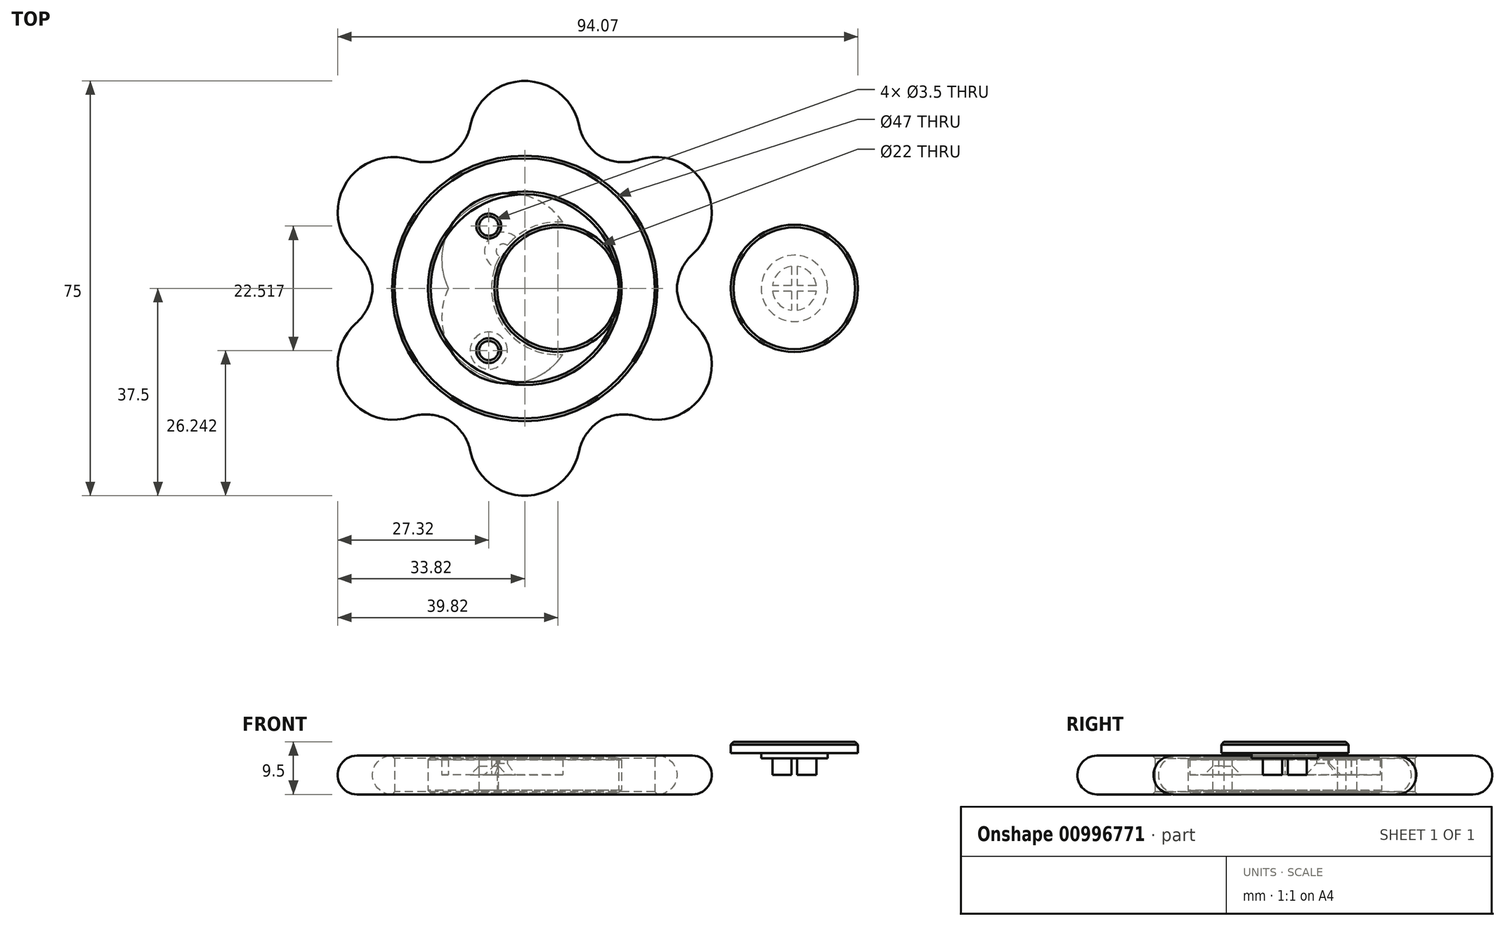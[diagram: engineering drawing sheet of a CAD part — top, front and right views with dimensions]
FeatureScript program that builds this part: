
annotation { "Feature Type Name" : "Feature", "Feature Type Description" : "" }
export const myFeature = defineFeature(function(context is Context, id is Id, definition is map)
    precondition{}
    {
        {
            var Q0;
            Q0=qCreatedBy(makeId("Top.planeOp"),FACE);
            var sketch = newSketch(context, id + "F0", { "sketchPlane" : qUnion([Q0])});
            skCircle(sketch, "E0", {"center": v(0, 0) * mm, "radius": 17.5 * mm});
            skCircle(sketch, "E1", {"center": v(6, 0) * mm, "radius": 11 * mm});
            skLineSegment(sketch, "E2", {"start": v(0, 0) * mm, "end": v(13.77, 19.66) * mm});
            skLineSegment(sketch, "E3", {"start": v(0, 0) * mm, "end": v(14.89, -21.26) * mm});
            skSolve(sketch);
        }
        {
            var Q0;
            Q0 = qSketchRegion(id + "F0", true);
            var Q1;
            {var subQ0=sQuery(id+"F0.wireOp",EDGE,"7888d7e4-cc9e-4509-8198-0eb2202acd58");var subQ1=sQuery(id+"F0.wireOp",EDGE,"E0");var subQ2=makeQuery(id+"F0.imprint","INTERSECT",VERTEX,{"derivedFrom":[subQ1,subQ0]});Q1=makeQuery(id+"F0.imprint","IMPRINT",FACE,{"disambiguationData":[TD([[makeQuery(id+"F0.imprint","IMPRINT",EDGE,{"disambiguationData":[TD([[subQ2,1.0]])],"derivedFrom":subQ1}),1.0]])]});}
            extrude(context, id + "F1", {"entities" : qUnion([Q0, Q1]), "depth" : 3.25 * mm, "offsetDistance" : 25 * mm, "hasSecondDirection" : true, "secondDirectionOppositeDirection" : true, "secondDirectionDepth" : 3.25 * mm});
        }
        {
            var Q0;
            Q0=qCreatedBy(makeId("Top.planeOp"),FACE);
            var sketch = newSketch(context, id + "F2", { "sketchPlane" : qUnion([Q0])});
            skCircle(sketch, "E4", {"center": v(0, 0) * mm, "radius": 23.5 * mm});
            skCircle(sketch, "E5", {"center": v(0, 0) * mm, "radius": 27.5 * mm});
            skArc(sketch, "E6", {"start": v(9.83, 25.68) * mm, "mid": v(0, 37.5) * mm, "end": v(-9.83, 25.68) * mm});
            skArc(sketch, "E7.1.0", {"start": v(-17.32, 21.36) * mm, "mid": v(-32.48, 18.75) * mm, "end": v(-27.16, 4.33) * mm});
            skArc(sketch, "E7.2.0", {"start": v(-27.16, -4.33) * mm, "mid": v(-32.48, -18.75) * mm, "end": v(-17.32, -21.36) * mm});
            skArc(sketch, "E7.3.0", {"start": v(-9.83, -25.68) * mm, "mid": v(0, -37.5) * mm, "end": v(9.83, -25.68) * mm});
            skArc(sketch, "E7.4.0", {"start": v(17.32, -21.36) * mm, "mid": v(32.48, -18.75) * mm, "end": v(27.16, -4.33) * mm});
            skArc(sketch, "E7.5.0", {"start": v(27.16, 4.33) * mm, "mid": v(32.48, 18.75) * mm, "end": v(17.32, 21.36) * mm});
            skPoint(sketch, "E8.orphan", {"position": v(8.33, 21.97) * mm});
            skPoint(sketch, "E9.orphan", {"position": v(-8.33, 21.97) * mm});
            skPoint(sketch, "E10.orphan", {"position": v(-14.86, 18.2) * mm});
            skPoint(sketch, "E11.orphan", {"position": v(-23.2, 3.77) * mm});
            skPoint(sketch, "E12.orphan", {"position": v(-23.2, -3.77) * mm});
            skPoint(sketch, "E13.orphan", {"position": v(-14.86, -18.2) * mm});
            skPoint(sketch, "E14.orphan", {"position": v(-8.33, -21.97) * mm});
            skPoint(sketch, "E15.orphan", {"position": v(8.33, -21.97) * mm});
            skPoint(sketch, "E16.orphan", {"position": v(14.86, -18.2) * mm});
            skPoint(sketch, "E17.orphan", {"position": v(23.2, -3.77) * mm});
            skPoint(sketch, "E18.orphan", {"position": v(23.2, 3.77) * mm});
            skPoint(sketch, "E19.orphan", {"position": v(14.86, 18.2) * mm});
            skSolve(sketch);
        }
        {
            var Q0;
            Q0 = qSketchRegion(id + "F2", true);
            extrude(context, id + "F3", {"entities" : qUnion([Q0]), "depth" : 3.5 * mm, "offsetDistance" : 25 * mm, "hasSecondDirection" : true, "secondDirectionOppositeDirection" : true, "secondDirectionDepth" : 3.5 * mm});
        }
        {
            var Q0;
            {var subQ0=sQuery(id+"F2.wireOp",EDGE,"E7.1.0");var subQ1=sQuery(id+"F2.wireOp",EDGE,"E5");Q0=makeQuery(id+"F3.opExtrude","SWEPT_EDGE",EDGE,{"disambiguationData":[OSD([subQ1,subQ0]),TDD([makeQuery(id+"F2.imprint","INTERSECT",VERTEX,{"disambiguationData":[OD(0.0)],"derivedFrom":[subQ1,subQ0]})])]});}
            var Q1;
            {var subQ0=sQuery(id+"F2.wireOp",EDGE,"E6");var subQ1=sQuery(id+"F2.wireOp",EDGE,"E5");Q1=makeQuery(id+"F3.opExtrude","SWEPT_EDGE",EDGE,{"disambiguationData":[OSD([subQ1,subQ0]),TDD([makeQuery(id+"F2.imprint","INTERSECT",VERTEX,{"disambiguationData":[OD(1.0)],"derivedFrom":[subQ1,subQ0]})])]});}
            var Q2;
            {var subQ0=sQuery(id+"F2.wireOp",EDGE,"E7.1.0");var subQ1=sQuery(id+"F2.wireOp",EDGE,"E5");Q2=makeQuery(id+"F3.opExtrude","SWEPT_EDGE",EDGE,{"disambiguationData":[OSD([subQ1,subQ0]),TDD([makeQuery(id+"F2.imprint","INTERSECT",VERTEX,{"disambiguationData":[OD(1.0)],"derivedFrom":[subQ1,subQ0]})])]});}
            var Q3;
            {var subQ0=sQuery(id+"F2.wireOp",EDGE,"E7.2.0");var subQ1=sQuery(id+"F2.wireOp",EDGE,"E5");Q3=makeQuery(id+"F3.opExtrude","SWEPT_EDGE",EDGE,{"disambiguationData":[OSD([subQ1,subQ0]),TDD([makeQuery(id+"F2.imprint","INTERSECT",VERTEX,{"disambiguationData":[OD(0.0)],"derivedFrom":[subQ1,subQ0]})])]});}
            var Q4;
            {var subQ0=sQuery(id+"F2.wireOp",EDGE,"E7.2.0");var subQ1=sQuery(id+"F2.wireOp",EDGE,"E5");Q4=makeQuery(id+"F3.opExtrude","SWEPT_EDGE",EDGE,{"disambiguationData":[OSD([subQ1,subQ0]),TDD([makeQuery(id+"F2.imprint","INTERSECT",VERTEX,{"disambiguationData":[OD(1.0)],"derivedFrom":[subQ1,subQ0]})])]});}
            var Q5;
            {var subQ0=sQuery(id+"F2.wireOp",EDGE,"E7.3.0");var subQ1=sQuery(id+"F2.wireOp",EDGE,"E5");Q5=makeQuery(id+"F3.opExtrude","SWEPT_EDGE",EDGE,{"disambiguationData":[OSD([subQ1,subQ0]),TDD([makeQuery(id+"F2.imprint","INTERSECT",VERTEX,{"disambiguationData":[OD(0.0)],"derivedFrom":[subQ1,subQ0]})])]});}
            var Q6;
            {var subQ0=sQuery(id+"F2.wireOp",EDGE,"E7.3.0");var subQ1=sQuery(id+"F2.wireOp",EDGE,"E5");Q6=makeQuery(id+"F3.opExtrude","SWEPT_EDGE",EDGE,{"disambiguationData":[OSD([subQ1,subQ0]),TDD([makeQuery(id+"F2.imprint","INTERSECT",VERTEX,{"disambiguationData":[OD(1.0)],"derivedFrom":[subQ1,subQ0]})])]});}
            var Q7;
            {var subQ0=sQuery(id+"F2.wireOp",EDGE,"E7.4.0");var subQ1=sQuery(id+"F2.wireOp",EDGE,"E5");Q7=makeQuery(id+"F3.opExtrude","SWEPT_EDGE",EDGE,{"disambiguationData":[OSD([subQ1,subQ0]),TDD([makeQuery(id+"F2.imprint","INTERSECT",VERTEX,{"disambiguationData":[OD(0.0)],"derivedFrom":[subQ1,subQ0]})])]});}
            var Q8;
            {var subQ0=sQuery(id+"F2.wireOp",EDGE,"E7.4.0");var subQ1=sQuery(id+"F2.wireOp",EDGE,"E5");Q8=makeQuery(id+"F3.opExtrude","SWEPT_EDGE",EDGE,{"disambiguationData":[OSD([subQ1,subQ0]),TDD([makeQuery(id+"F2.imprint","INTERSECT",VERTEX,{"disambiguationData":[OD(1.0)],"derivedFrom":[subQ1,subQ0]})])]});}
            var Q9;
            {var subQ0=sQuery(id+"F2.wireOp",EDGE,"E7.5.0");var subQ1=sQuery(id+"F2.wireOp",EDGE,"E5");Q9=makeQuery(id+"F3.opExtrude","SWEPT_EDGE",EDGE,{"disambiguationData":[OSD([subQ1,subQ0]),TDD([makeQuery(id+"F2.imprint","INTERSECT",VERTEX,{"disambiguationData":[OD(0.0)],"derivedFrom":[subQ1,subQ0]})])]});}
            var Q10;
            {var subQ0=sQuery(id+"F2.wireOp",EDGE,"E7.5.0");var subQ1=sQuery(id+"F2.wireOp",EDGE,"E5");Q10=makeQuery(id+"F3.opExtrude","SWEPT_EDGE",EDGE,{"disambiguationData":[OSD([subQ1,subQ0]),TDD([makeQuery(id+"F2.imprint","INTERSECT",VERTEX,{"disambiguationData":[OD(1.0)],"derivedFrom":[subQ1,subQ0]})])]});}
            var Q11;
            {var subQ0=sQuery(id+"F2.wireOp",EDGE,"E6");var subQ1=sQuery(id+"F2.wireOp",EDGE,"E5");Q11=makeQuery(id+"F3.opExtrude","SWEPT_EDGE",EDGE,{"disambiguationData":[OSD([subQ1,subQ0]),TDD([makeQuery(id+"F2.imprint","INTERSECT",VERTEX,{"disambiguationData":[OD(0.0)],"derivedFrom":[subQ1,subQ0]})])]});}
            fillet(context, id + "F4", {"entities" : qUnion([Q0, Q1, Q2, Q3, Q4, Q5, Q6, Q7, Q8, Q9, Q10, Q11]), "tangentPropagation" : true, "radius" : 9 * mm, "defaultsChanged" : true, "vertexSettings" : [], "allowEdgeOverflow" : false});
        }
        {
            var Q0;
            Q0=makeQuery(id+"F3.opExtrude","SWEPT_FACE",FACE,{"disambiguationData":[OSD([sQuery(id+"F2.wireOp",EDGE,"E7.5.0")])]});
            var Q1;
            Q1=makeQuery(id+"F3.opExtrude","SWEPT_FACE",FACE,{"disambiguationData":[OSD([sQuery(id+"F2.wireOp",EDGE,"E6")])]});
            var Q2;
            {var subQ0=sQuery(id+"F2.wireOp",EDGE,"E7.5.0");var subQ1=sQuery(id+"F2.wireOp",EDGE,"E5");Q2=makeQuery(id+"F4.opFillet","BLEND_FACE",FACE,{"disambiguationData":[OSD([subQ1,subQ0]),TDD([makeQuery(id+"F3.opExtrude","SWEPT_EDGE",EDGE,{"disambiguationData":[OSD([subQ1,subQ0]),TDD([makeQuery(id+"F2.imprint","INTERSECT",VERTEX,{"disambiguationData":[OD(1.0)],"derivedFrom":[subQ1,subQ0]})])]})])]});}
            var Q3;
            {var subQ0=sQuery(id+"F2.wireOp",EDGE,"E6");var subQ1=sQuery(id+"F2.wireOp",EDGE,"E5");Q3=makeQuery(id+"F4.opFillet","BLEND_FACE",FACE,{"disambiguationData":[OSD([subQ1,subQ0]),TDD([makeQuery(id+"F3.opExtrude","SWEPT_EDGE",EDGE,{"disambiguationData":[OSD([subQ1,subQ0]),TDD([makeQuery(id+"F2.imprint","INTERSECT",VERTEX,{"disambiguationData":[OD(0.0)],"derivedFrom":[subQ1,subQ0]})])]})])]});}
            var Q4;
            {var subQ0=sQuery(id+"F2.wireOp",EDGE,"E7.1.0");var subQ1=sQuery(id+"F2.wireOp",EDGE,"E5");Q4=makeQuery(id+"F4.opFillet","BLEND_FACE",FACE,{"disambiguationData":[OSD([subQ1,subQ0]),TDD([makeQuery(id+"F3.opExtrude","SWEPT_EDGE",EDGE,{"disambiguationData":[OSD([subQ1,subQ0]),TDD([makeQuery(id+"F2.imprint","INTERSECT",VERTEX,{"disambiguationData":[OD(0.0)],"derivedFrom":[subQ1,subQ0]})])]})])]});}
            var Q5;
            {var subQ0=sQuery(id+"F2.wireOp",EDGE,"E6");var subQ1=sQuery(id+"F2.wireOp",EDGE,"E5");Q5=makeQuery(id+"F4.opFillet","BLEND_FACE",FACE,{"disambiguationData":[OSD([subQ1,subQ0]),TDD([makeQuery(id+"F3.opExtrude","SWEPT_EDGE",EDGE,{"disambiguationData":[OSD([subQ1,subQ0]),TDD([makeQuery(id+"F2.imprint","INTERSECT",VERTEX,{"disambiguationData":[OD(1.0)],"derivedFrom":[subQ1,subQ0]})])]})])]});}
            var Q6;
            Q6=makeQuery(id+"F3.opExtrude","SWEPT_FACE",FACE,{"disambiguationData":[OSD([sQuery(id+"F2.wireOp",EDGE,"E7.1.0")])]});
            var Q7;
            {var subQ0=sQuery(id+"F2.wireOp",EDGE,"E7.2.0");var subQ1=sQuery(id+"F2.wireOp",EDGE,"E5");Q7=makeQuery(id+"F4.opFillet","BLEND_FACE",FACE,{"disambiguationData":[OSD([subQ1,subQ0]),TDD([makeQuery(id+"F3.opExtrude","SWEPT_EDGE",EDGE,{"disambiguationData":[OSD([subQ1,subQ0]),TDD([makeQuery(id+"F2.imprint","INTERSECT",VERTEX,{"disambiguationData":[OD(0.0)],"derivedFrom":[subQ1,subQ0]})])]})])]});}
            var Q8;
            {var subQ0=sQuery(id+"F2.wireOp",EDGE,"E7.1.0");var subQ1=sQuery(id+"F2.wireOp",EDGE,"E5");Q8=makeQuery(id+"F4.opFillet","BLEND_FACE",FACE,{"disambiguationData":[OSD([subQ1,subQ0]),TDD([makeQuery(id+"F3.opExtrude","SWEPT_EDGE",EDGE,{"disambiguationData":[OSD([subQ1,subQ0]),TDD([makeQuery(id+"F2.imprint","INTERSECT",VERTEX,{"disambiguationData":[OD(1.0)],"derivedFrom":[subQ1,subQ0]})])]})])]});}
            var Q9;
            Q9=makeQuery(id+"F3.opExtrude","SWEPT_FACE",FACE,{"disambiguationData":[OSD([sQuery(id+"F2.wireOp",EDGE,"E7.2.0")])]});
            var Q10;
            {var subQ0=sQuery(id+"F2.wireOp",EDGE,"E7.2.0");var subQ1=sQuery(id+"F2.wireOp",EDGE,"E5");Q10=makeQuery(id+"F4.opFillet","BLEND_FACE",FACE,{"disambiguationData":[OSD([subQ1,subQ0]),TDD([makeQuery(id+"F3.opExtrude","SWEPT_EDGE",EDGE,{"disambiguationData":[OSD([subQ1,subQ0]),TDD([makeQuery(id+"F2.imprint","INTERSECT",VERTEX,{"disambiguationData":[OD(1.0)],"derivedFrom":[subQ1,subQ0]})])]})])]});}
            var Q11;
            Q11=makeQuery(id+"F3.opExtrude","SWEPT_FACE",FACE,{"disambiguationData":[OSD([sQuery(id+"F2.wireOp",EDGE,"E7.3.0")])]});
            var Q12;
            {var subQ0=sQuery(id+"F2.wireOp",EDGE,"E7.3.0");var subQ1=sQuery(id+"F2.wireOp",EDGE,"E5");Q12=makeQuery(id+"F4.opFillet","BLEND_FACE",FACE,{"disambiguationData":[OSD([subQ1,subQ0]),TDD([makeQuery(id+"F3.opExtrude","SWEPT_EDGE",EDGE,{"disambiguationData":[OSD([subQ1,subQ0]),TDD([makeQuery(id+"F2.imprint","INTERSECT",VERTEX,{"disambiguationData":[OD(0.0)],"derivedFrom":[subQ1,subQ0]})])]})])]});}
            var Q13;
            {var subQ0=sQuery(id+"F2.wireOp",EDGE,"E7.3.0");var subQ1=sQuery(id+"F2.wireOp",EDGE,"E5");Q13=makeQuery(id+"F4.opFillet","BLEND_FACE",FACE,{"disambiguationData":[OSD([subQ1,subQ0]),TDD([makeQuery(id+"F3.opExtrude","SWEPT_EDGE",EDGE,{"disambiguationData":[OSD([subQ1,subQ0]),TDD([makeQuery(id+"F2.imprint","INTERSECT",VERTEX,{"disambiguationData":[OD(1.0)],"derivedFrom":[subQ1,subQ0]})])]})])]});}
            var Q14;
            {var subQ0=sQuery(id+"F2.wireOp",EDGE,"E7.4.0");var subQ1=sQuery(id+"F2.wireOp",EDGE,"E5");Q14=makeQuery(id+"F4.opFillet","BLEND_FACE",FACE,{"disambiguationData":[OSD([subQ1,subQ0]),TDD([makeQuery(id+"F3.opExtrude","SWEPT_EDGE",EDGE,{"disambiguationData":[OSD([subQ1,subQ0]),TDD([makeQuery(id+"F2.imprint","INTERSECT",VERTEX,{"disambiguationData":[OD(0.0)],"derivedFrom":[subQ1,subQ0]})])]})])]});}
            var Q15;
            Q15=makeQuery(id+"F3.opExtrude","SWEPT_FACE",FACE,{"disambiguationData":[OSD([sQuery(id+"F2.wireOp",EDGE,"E7.4.0")])]});
            var Q16;
            {var subQ0=sQuery(id+"F2.wireOp",EDGE,"E7.4.0");var subQ1=sQuery(id+"F2.wireOp",EDGE,"E5");Q16=makeQuery(id+"F4.opFillet","BLEND_FACE",FACE,{"disambiguationData":[OSD([subQ1,subQ0]),TDD([makeQuery(id+"F3.opExtrude","SWEPT_EDGE",EDGE,{"disambiguationData":[OSD([subQ1,subQ0]),TDD([makeQuery(id+"F2.imprint","INTERSECT",VERTEX,{"disambiguationData":[OD(1.0)],"derivedFrom":[subQ1,subQ0]})])]})])]});}
            var Q17;
            {var subQ0=sQuery(id+"F2.wireOp",EDGE,"E7.5.0");var subQ1=sQuery(id+"F2.wireOp",EDGE,"E5");Q17=makeQuery(id+"F4.opFillet","BLEND_FACE",FACE,{"disambiguationData":[OSD([subQ1,subQ0]),TDD([makeQuery(id+"F3.opExtrude","SWEPT_EDGE",EDGE,{"disambiguationData":[OSD([subQ1,subQ0]),TDD([makeQuery(id+"F2.imprint","INTERSECT",VERTEX,{"disambiguationData":[OD(0.0)],"derivedFrom":[subQ1,subQ0]})])]})])]});}
            fillet(context, id + "F5", {"entities" : qUnion([Q0, Q1, Q2, Q3, Q4, Q5, Q6, Q7, Q8, Q9, Q10, Q11, Q12, Q13, Q14, Q15, Q16, Q17]), "tangentPropagation" : true, "radius" : 3.5 * mm, "defaultsChanged" : false, "vertexSettings" : [], "allowEdgeOverflow" : false});
        }
        {
            var Q0;
            Q0=qCreatedBy(makeId("Top.planeOp"),FACE);
            var sketch = newSketch(context, id + "F6", { "sketchPlane" : qUnion([Q0])});
            skLineSegment(sketch, "E20", {"start": v(0, -24.5) * mm, "end": v(35, 0) * mm});
            skLineSegment(sketch, "E21", {"start": v(35, 0) * mm, "end": v(0, 24.5) * mm});
            skSolve(sketch);
        }
        {
            var Q0;
            Q0 = qSketchRegion(id + "F6", true);
            var Q1;
            Q1=sQuery(id+"F6.wireOp",EDGE,"E21");
            var Q2;
            Q2=sQuery(id+"F6.wireOp",EDGE,"E20");
            extrude(context, id + "F7", {"entities" : qUnion([Q0]), "bodyType" : ToolBodyType.SURFACE, "surfaceEntities" : qUnion([Q1, Q2]), "depth" : 3.5 * mm, "offsetDistance" : 25 * mm, "hasSecondDirection" : true, "secondDirectionOppositeDirection" : true, "secondDirectionDepth" : 3.5 * mm});
        }
        {
            var Q0;
            Q0=makeQuery(id+"F7.opExtrude","SWEPT_FACE",FACE,{"disambiguationData":[OSD([sQuery(id+"F6.wireOp",EDGE,"E21")])]});
            var sketch = newSketch(context, id + "F8", { "sketchPlane" : qUnion([Q0])});
            skPoint(sketch, "E22", {"position": v(0, 0) * mm});
            skSolve(sketch);
        }
        {
            var Q0;
            Q0=makeQuery(id+"F7.opExtrude","SWEPT_FACE",FACE,{"disambiguationData":[OSD([sQuery(id+"F6.wireOp",EDGE,"E20")])]});
            var sketch = newSketch(context, id + "F9", { "sketchPlane" : qUnion([Q0])});
            skPoint(sketch, "E23", {"position": v(0, 0) * mm});
            skSolve(sketch);
        }
        {
            var Q0;
            Q0=qCreatedBy(makeId("Top.planeOp"),FACE);
            var sketch = newSketch(context, id + "F10", { "sketchPlane" : qUnion([Q0])});
            skArc(sketch, "E24", {"start": v(6.9, 11.97) * mm, "mid": v(-6, 0) * mm, "end": v(6.9, -11.97) * mm});
            skArc(sketch, "E25.1.0", {"start": v(6.9, 11.97) * mm, "mid": v(-9, 15.59) * mm, "end": v(-13.82, 0) * mm});
            skArc(sketch, "E25.2.0", {"start": v(-13.82, 0) * mm, "mid": v(-9, -15.59) * mm, "end": v(6.9, -11.97) * mm});
            skPoint(sketch, "E25.center", {"position": v(0, 0) * mm});
            skLineSegment(sketch, "E26", {"start": v(-6.5, -11.26) * mm, "end": v(-3.9, -6.77) * mm});
            skLineSegment(sketch, "E27", {"start": v(-6.5, 11.26) * mm, "end": v(-3.9, 6.77) * mm});
            skSolve(sketch);
        }
        {
            var Q0;
            {var subQ0=sQuery(id+"F10.wireOp",EDGE,"E25.1.0");Q0=makeQuery(id+"F10.imprint","IMPRINT",FACE,{"disambiguationData":[TD([[makeQuery(id+"F10.imprint","IMPRINT",EDGE,{"derivedFrom":subQ0}),1.0]])]});}
            extrude(context, id + "F11", {"entities" : qUnion([Q0]), "depth" : 3 * mm, "offsetDistance" : 25 * mm});
        }
        {
            var Q0;
            Q0=sQuery(id+"F10.wireOp",VERTEX,"E27.end");
            var Q1;
            Q1=sQuery(id+"F10.wireOp",VERTEX,"E26.start");
            var Q2;
            Q2=makeQuery(id+"F11.opExtrude","SWEPT_BODY",BODY,{"disambiguationData":[OSD([sQuery(id+"F10.wireOp",EDGE,"E24"),sQuery(id+"F10.wireOp",EDGE,"E25.1.0"),sQuery(id+"F10.wireOp",EDGE,"E25.2.0")])]});
            hole(context, id + "F12", {"style" : HoleStyle.C_SINK, "endStyle" : HoleEndStyle.BLIND, "oppositeDirection" : true, "standardTappedOrClearance" : lookupTablePath({ "standard" : "ISO", "engagement" : "75%", "pitch" : "0.5 mm", "size" : "M3", "type" : "Tapped" }), "standardBlindInLast" : lookupTablePath({ "standard" : "ISO", "fit" : "Normal", "engagement" : "75%", "pitch" : "0.5 mm", "size" : "M3", "type" : "Clearance & tapped" }), "holeDiameter" : 2.5 * mm, "cSinkDiameter" : 6.72 * mm, "cSinkAngle" : 90 * degree, "majorDiameter" : 3 * mm, "showTappedDepth" : true, "holeDepth" : 13.5 * mm, "isTappedThrough" : true, "tappedDepth" : 12 * mm, "tapClearance" : 3, "startFromSketch" : true, "locations" : qUnion([Q0, Q1]), "scope" : qUnion([Q2])});
        }
        {
            var Q0;
            Q0=makeQuery(id+"F1.opExtrude","CAP_FACE",FACE,{"disambiguationData":[OSD([sQuery(id+"F0.wireOp",EDGE,"E0"),sQuery(id+"F0.wireOp",EDGE,"E1")])],"isStart":false});
            var sketch = newSketch(context, id + "F13", { "sketchPlane" : qUnion([Q0])});
            skCircle(sketch, "E28", {"center": v(-6.5, 11.26) * mm, "radius": 1.75 * mm});
            skCircle(sketch, "E29", {"center": v(-6.5, -11.26) * mm, "radius": 1.75 * mm});
            skSolve(sketch);
        }
        {
            var Q0;
            Q0 = qSketchRegion(id + "F13", true);
            extrude(context, id + "F14", {"entities" : qUnion([Q0]), "operationType" : NewBodyOperationType.REMOVE, "endBound" : BoundingType.THROUGH_ALL, "oppositeDirection" : true, "depth" : 25 * mm, "offsetDistance" : 25 * mm});
        }
        {
            var Q0;
            Q0=qCreatedBy(makeId("Front.planeOp"),FACE);
            var sketch = newSketch(context, id + "F15", { "sketchPlane" : qUnion([Q0])});
            skLineSegment(sketch, "E30", {"start": v(44.75, 0) * mm, "end": v(44.75, 3) * mm});
            skLineSegment(sketch, "E31", {"start": v(44.75, 3) * mm, "end": v(42.75, 3) * mm});
            skLineSegment(sketch, "E32", {"start": v(42.75, 3) * mm, "end": v(42.75, 4) * mm});
            skLineSegment(sketch, "E33", {"start": v(42.75, 4) * mm, "end": v(37.25, 4) * mm});
            skLineSegment(sketch, "E34", {"start": v(37.25, 4) * mm, "end": v(37.25, 6) * mm});
            skLineSegment(sketch, "E35", {"start": v(37.25, 6) * mm, "end": v(48.75, 6) * mm});
            skLineSegment(sketch, "E36", {"start": v(48.75, 6) * mm, "end": v(48.75, 0) * mm});
            skLineSegment(sketch, "E37", {"start": v(48.75, 0) * mm, "end": v(44.75, 0) * mm});
            skSolve(sketch);
        }
        {
            var Q0;
            Q0=makeQuery(id+"F15.imprint","IMPRINT",FACE,{"disambiguationData":[TD([[makeQuery(id+"F15.imprint","IMPRINT",EDGE,{"derivedFrom":sQuery(id+"F15.wireOp",EDGE,"E30")}),-1.0]])]});
            var Q1;
            Q1=sQuery(id+"F15.wireOp",EDGE,"E36");
            revolve(context, id + "F16", {"surfaceOperationType" : NewSurfaceOperationType.NEW, "entities" : qUnion([Q0]), "axis" : qUnion([Q1]), "revolveType" : RevolveType.FULL});
        }
        {
            var Q0;
            Q0=makeQuery(id+"F16.opRevolve","SWEPT_FACE",FACE,{"disambiguationData":[OSD([sQuery(id+"F15.wireOp",EDGE,"E37")])]});
            var sketch = newSketch(context, id + "F17", { "sketchPlane" : qUnion([Q0])});
            skLineSegment(sketch, "E38.bottom", {"start": v(49.25, -5) * mm, "end": v(48.25, -5) * mm});
            skLineSegment(sketch, "E38.top", {"start": v(49.25, 5) * mm, "end": v(48.25, 5) * mm});
            skLineSegment(sketch, "E38.left", {"start": v(49.25, -5) * mm, "end": v(49.25, -0.5) * mm});
            skLineSegment(sketch, "E38.right", {"start": v(48.25, -5) * mm, "end": v(48.25, -0.5) * mm});
            skPoint(sketch, "E38.middle", {"position": v(48.75, 0) * mm});
            skLineSegment(sketch, "E39.bottom", {"start": v(53.75, 0.5) * mm, "end": v(49.25, 0.5) * mm});
            skLineSegment(sketch, "E39.top", {"start": v(53.75, -0.5) * mm, "end": v(49.25, -0.5) * mm});
            skLineSegment(sketch, "E39.left", {"start": v(53.75, 0.5) * mm, "end": v(53.75, -0.5) * mm});
            skLineSegment(sketch, "E39.right", {"start": v(43.75, 0.5) * mm, "end": v(43.75, -0.5) * mm});
            skLineSegment(sketch, "E40.trimOffspring", {"start": v(49.25, 0.5) * mm, "end": v(49.25, 5) * mm});
            skLineSegment(sketch, "E41.trimOffspring", {"start": v(48.25, 0.5) * mm, "end": v(48.25, 5) * mm});
            skLineSegment(sketch, "E42.trimOffspring", {"start": v(48.25, 0.5) * mm, "end": v(43.75, 0.5) * mm});
            skLineSegment(sketch, "E43.trimOffspring", {"start": v(48.25, -0.5) * mm, "end": v(43.75, -0.5) * mm});
            skSolve(sketch);
        }
        {
            var Q0;
            Q0 = qSketchRegion(id + "F17", true);
            extrude(context, id + "F18", {"entities" : qUnion([Q0]), "operationType" : NewBodyOperationType.REMOVE, "oppositeDirection" : true, "depth" : 3 * mm, "offsetDistance" : 25 * mm});
        }
        {
            var Q0;
            Q0=makeQuery(id+"F16.opRevolve","SWEPT_FACE",FACE,{"disambiguationData":[OSD([sQuery(id+"F15.wireOp",EDGE,"E35")])]});
            var Q1;
            Q1=makeQuery(id+"F11.opExtrude","CAP_FACE",FACE,{"disambiguationData":[OSD([sQuery(id+"F10.wireOp",EDGE,"E24"),sQuery(id+"F10.wireOp",EDGE,"E25.1.0"),sQuery(id+"F10.wireOp",EDGE,"E25.2.0")])],"isStart":true});
            var Q2;
            Q2=makeQuery(id+"F1.opExtrude","CAP_FACE",FACE,{"disambiguationData":[OSD([sQuery(id+"F0.wireOp",EDGE,"E0"),sQuery(id+"F0.wireOp",EDGE,"E1")])],"isStart":true});
            var Q3;
            Q3=makeQuery(id+"F1.opExtrude","CAP_FACE",FACE,{"disambiguationData":[OSD([sQuery(id+"F0.wireOp",EDGE,"E0"),sQuery(id+"F0.wireOp",EDGE,"E1")])],"isStart":false});
            var Q4;
            Q4=makeQuery(id+"F3.opExtrude","CAP_FACE",FACE,{"disambiguationData":[OSD([sQuery(id+"F2.wireOp",EDGE,"E4"),sQuery(id+"F2.wireOp",EDGE,"E5"),sQuery(id+"F2.wireOp",EDGE,"E6"),sQuery(id+"F2.wireOp",EDGE,"E7.1.0"),sQuery(id+"F2.wireOp",EDGE,"E7.2.0"),sQuery(id+"F2.wireOp",EDGE,"E7.3.0"),sQuery(id+"F2.wireOp",EDGE,"E7.4.0"),sQuery(id+"F2.wireOp",EDGE,"E7.5.0")])],"isStart":false});
            var Q5;
            Q5=makeQuery(id+"F3.opExtrude","CAP_FACE",FACE,{"disambiguationData":[OSD([sQuery(id+"F2.wireOp",EDGE,"E4"),sQuery(id+"F2.wireOp",EDGE,"E5"),sQuery(id+"F2.wireOp",EDGE,"E6"),sQuery(id+"F2.wireOp",EDGE,"E7.1.0"),sQuery(id+"F2.wireOp",EDGE,"E7.2.0"),sQuery(id+"F2.wireOp",EDGE,"E7.3.0"),sQuery(id+"F2.wireOp",EDGE,"E7.4.0"),sQuery(id+"F2.wireOp",EDGE,"E7.5.0")])],"isStart":true});
            chamfer(context, id + "F19", {"entities" : qUnion([Q0, Q1, Q2, Q3, Q4, Q5]), "width" : 0.5 * mm, "tangentPropagation" : true});
        }
    });
